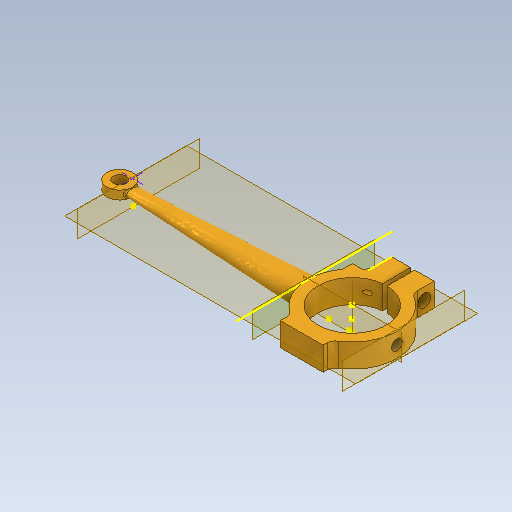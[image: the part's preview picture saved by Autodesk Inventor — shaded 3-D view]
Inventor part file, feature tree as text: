
AUTODESK INVENTOR PART (.ipt)
format: ipt  version: 2020 (Build 240168000, 168)  size: 406,016 bytes
history: native  units: mm
features: sketch x24, extrude x9, plane x5, fillet x3, hole x2, thread x1, loft x1, other x1
ambient origin geometry x8: Origin, YZ Plane, XZ Plane, XY Plane, X Axis, Y Axis, Z Axis, Center Point
bodies: Solid1 (feature_tree)
feature tree (46):
  extrude  "Extrusion1"  Depth=10.0mm
  plane  "Work Plane1"
  sketch  "Sketch2"  dims[d2=14.5mm d3=16.0mm]
  plane  "Work Plane2"
  sketch  "Sketch4"  dims[d4=21.0mm d5=5.5mm d6=0.0mm]
  sketch  "Sketch11"  dims[d7=0.0mm d37=3.0mm d38=2.27mm]
  sketch  "Sketch12"  dims[d39=2.75mm d40=4.5mm d41=0.0mm]
  extrude  "Extrusion7"  Depth=16.0mm
  extrude  "Extrusion8"  Depth=5.5mm TaperAngle=0.0deg
  sketch  "Sketch18"  dims[d51=2.0mm d53=2.3mm]
  extrude  "Extrusion9"  Depth=3.0mm
  sketch  "Sketch20"  dims[d57=1.3mm d58=2.75mm]
  sketch  "Sketch21"  dims[d59=1.0mm d60=6.0mm d61=2.0mm d62=2.0mm d63=15.0deg d64=5.52mm d65=20.594885mm d66=2.75mm d67=2.75mm]
  fillet  "Fillet1"  Radius=2.27mm
  sketch  "Sketch22"  dims[d68=2.5mm d69=6.0mm d70=2.0mm d71=2.0mm d72=15.0deg d73=2.56mm d74=20.594885mm d75=2.5mm d76=0.0mm d77=3.5mm]
  sketch  "Sketch23"  dims[d78=2.5mm]
  extrude  "Extrusion10"  Depth=4.5mm TaperAngle=0.0deg
  hole  "Hole1"  [1 undecoded]
  plane  "Work Plane5"
  hole  "Hole2"  [1 undecoded]
  thread  "Thread1"  [1 undecoded]
  plane  "Work Plane7"
  sketch  "Sketch27"  dims[d84=0.0mm d85=90.0deg]
  plane  "Work Plane8"
  sketch  "Sketch28"  dims[d86=0.0mm d87=90.0deg]
  loft  "Loft2"
  sketch  "Sketch29"  dims[d88=6.0mm]
  extrude  "Extrusion11"  Depth=2.0mm
  extrude  "Extrusion12"  Depth=2.75mm
  sketch  "Sketch32"  dims[d92=3.0mm]
  extrude  "Extrusion13"  Depth=2.75mm
  fillet  "Fillet2"  Radius=2.75mm
  extrude  "Extrusion14"  Depth=2.5mm TaperAngle=0.0deg
  fillet  "Fillet3"  Radius=3.5mm
  sketch  "Sketch1"  dims[d0=26.0mm d1=10.0mm]
  other  "Work Axis1"
  sketch  "Sketch16"  dims[d42=4.5mm d43=0.0mm d44=1.0mm]
  sketch  "Sketch17"  dims[d45=4.5mm d46=5.5mm d47=10.0mm d48=0.0mm]
  sketch  "Sketch19"  dims[d54=5.5mm d55=0.0mm d56=2.0mm]
  sketch  "Sketch24"  dims[d81=51.5mm]
  sketch  "Sketch25"  dims[d82=0.75mm]
  sketch  "Sketch26"  dims[d83=1.5mm]
  sketch  "Sketch30"  dims[d89=54.5mm]
  sketch  "Sketch31"  dims[d90=2.0mm d91=0.0mm]
  sketch  "Sketch33"  dims[d93=0.0mm d94=0.0mm]
  sketch  "Sketch34"  dims[d95=1.0mm d96=0.0mm d97=0.5mm d98=1.0mm d99=0.0mm d100=0.5mm d8=0.872665mm]
note: 3 required parameter values undecoded (feature->parameter linkage not recoverable at this tier; creation-order binding heuristic only, values carry confidence <= 0.55)
